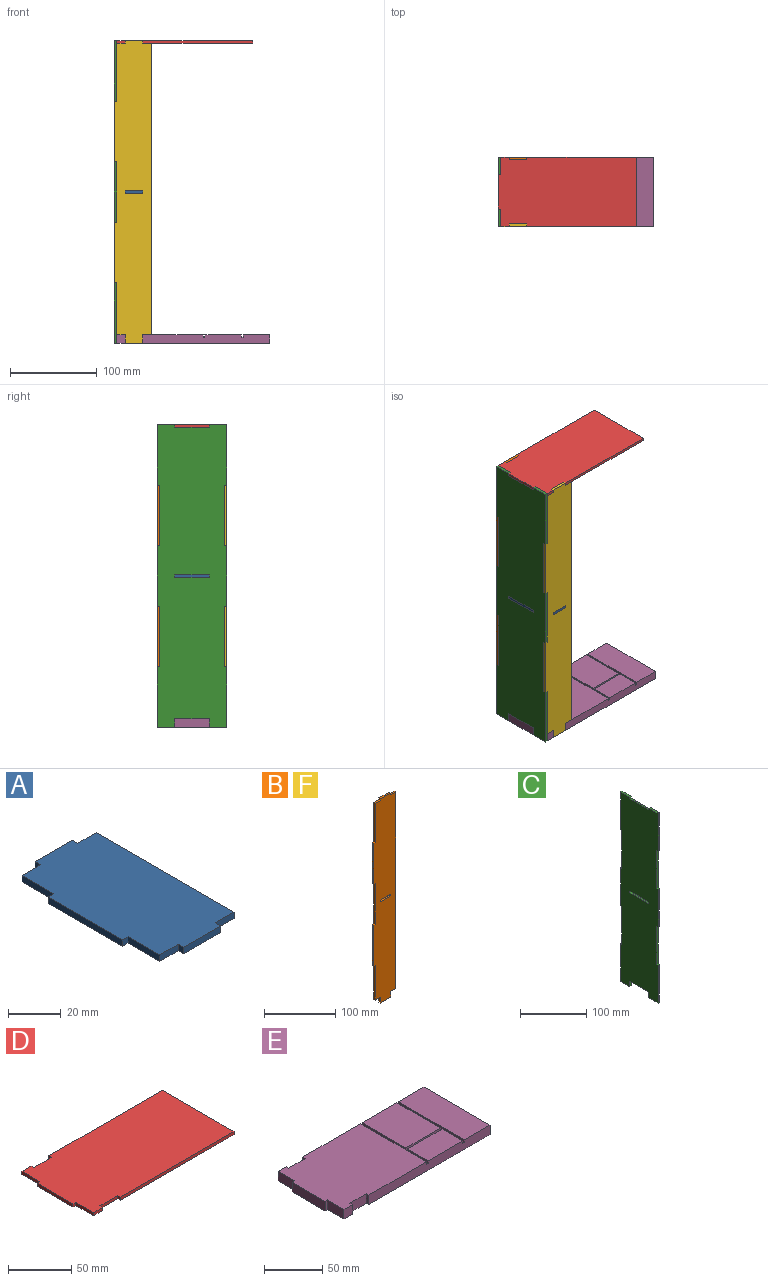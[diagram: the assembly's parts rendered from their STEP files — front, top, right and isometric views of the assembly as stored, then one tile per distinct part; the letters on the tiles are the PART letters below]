
ASSEMBLY  parts=6 mates=5
PART A: 18 faces, bbox 43x80x3 mm
  f0: plane 10x3mm, normal (0,-1,0), area 30mm2, adj f1,f15,f16,f17
  f1: plane 3x3mm, normal (-1,0,0), area 9mm2, adj f0,f2,f16,f17
  f2: plane 20x3mm, normal (0,-1,0), area 60mm2, adj f1,f3,f16,f17
  f3: plane 3x3mm, normal (1,0,0), area 9mm2, adj f2,f4,f16,f17
  f4: plane 10x3mm, normal (0,-1,0), area 30mm2, adj f3,f5,f16,f17
  f5: plane 74x3mm, normal (1,0,0), area 222mm2, adj f4,f6,f16,f17
  f6: plane 10x3mm, normal (0,1,0), area 30mm2, adj f5,f7,f16,f17
  f7: plane 3x3mm, normal (1,0,0), area 9mm2, adj f6,f8,f16,f17
  f8: plane 20x3mm, normal (0,1,0), area 60mm2, adj f7,f9,f16,f17
  f9: plane 3x3mm, normal (-1,0,0), area 9mm2, adj f8,f10,f16,f17
  f10: plane 10x3mm, normal (0,1,0), area 30mm2, adj f9,f11,f16,f17
  f11: plane 17x3mm, normal (-1,0,0), area 51mm2, adj f10,f12,f16,f17
  f12: plane 3x3mm, normal (0,1,0), area 9mm2, adj f11,f13,f16,f17
  f13: plane 40x3mm, normal (-1,0,0), area 120mm2, adj f12,f14,f16,f17
  f14: plane 3x3mm, normal (0,-1,0), area 9mm2, adj f13,f15,f16,f17
  f15: plane 17x3mm, normal (-1,0,0), area 51mm2, adj f0,f14,f16,f17
  f16: plane 80x43mm, normal (0,0,1), area 3200mm2, adj f0,f1,f2,f3,f4,f5,f6,f7
  f17: plane 80x43mm, normal (0,0,-1), area 3200mm2, adj f0,f1,f2,f3,f4,f5,f6,f7
PART B: 26 faces, bbox 43x3x350 mm
  f0: plane 10x3mm, normal (-1,0,0), area 30mm2, adj f1,f23,f24,f25
  f1: plane 20x3mm, normal (0,0,-1), area 60mm2, adj f0,f2,f24,f25
  f2: plane 10x3mm, normal (1,0,0), area 30mm2, adj f1,f3,f24,f25
  f3: plane 10x3mm, normal (0,0,-1), area 30mm2, adj f2,f4,f24,f25
  f4: plane 337x3mm, normal (1,0,0), area 1011mm2, adj f3,f5,f24,f25
  f5: plane 10x3mm, normal (0,0,1), area 30mm2, adj f4,f6,f24,f25
  f6: plane 3x3mm, normal (1,0,0), area 9mm2, adj f5,f7,f24,f25
  f7: plane 20x3mm, normal (0,0,1), area 60mm2, adj f6,f8,f24,f25
  f8: plane 3x3mm, normal (-1,0,0), area 9mm2, adj f7,f9,f24,f25
  f9: plane 10x3mm, normal (0,0,1), area 30mm2, adj f8,f10,f24,f25
  f10: plane 67x3mm, normal (-1,0,0), area 201mm2, adj f9,f11,f24,f25
  f11: plane 3x3mm, normal (0,0,1), area 9mm2, adj f10,f12,f24,f25
  f12: plane 70x3mm, normal (-1,0,0), area 210mm2, adj f11,f13,f24,f25
  f13: plane 3x3mm, normal (0,0,-1), area 9mm2, adj f12,f14,f24,f25
  f14: plane 70x3mm, normal (-1,0,0), area 210mm2, adj f13,f15,f24,f25
  f15: plane 3x3mm, normal (0,0,1), area 9mm2, adj f14,f16,f24,f25
  f16: plane 70x3mm, normal (-1,0,0), area 210mm2, adj f15,f17,f24,f25
  f17: plane 3x3mm, normal (0,0,-1), area 9mm2, adj f16,f18,f24,f25
  f18: plane 60x3mm, normal (-1,0,0), area 180mm2, adj f17,f23,f24,f25
  f19: plane 20x3mm, normal (0,0,-1), area 60mm2, adj f20,f22,f24,f25
  f20: plane 3x3mm, normal (-1,0,0), area 9mm2, adj f19,f21,f24,f25
  f21: plane 20x3mm, normal (0,0,1), area 60mm2, adj f20,f22,f24,f25
  f22: plane 3x3mm, normal (1,0,0), area 9mm2, adj f19,f21,f24,f25
  f23: plane 10x3mm, normal (0,0,-1), area 30mm2, adj f0,f18,f24,f25
  f24: plane 350x43mm, normal (0,1,0), area 14100mm2, adj f0,f1,f2,f3,f4,f5,f6,f7
  f25: plane 350x43mm, normal (0,-1,0), area 14100mm2, adj f0,f1,f2,f3,f4,f5,f6,f7
PART C: 34 faces, bbox 3x80x350 mm
  f0: plane 3x3mm, normal (0,1,0), area 9mm2, adj f1,f31,f32,f33
  f1: plane 20x3mm, normal (0,0,1), area 60mm2, adj f0,f2,f32,f33
  f2: plane 70x3mm, normal (0,-1,0), area 210mm2, adj f1,f3,f32,f33
  f3: plane 3x3mm, normal (0,0,-1), area 9mm2, adj f2,f4,f32,f33
  f4: plane 70x3mm, normal (0,-1,0), area 210mm2, adj f3,f5,f32,f33
  f5: plane 3x3mm, normal (0,0,1), area 9mm2, adj f4,f6,f32,f33
  f6: plane 70x3mm, normal (0,-1,0), area 210mm2, adj f5,f7,f32,f33
  f7: plane 3x3mm, normal (0,0,-1), area 9mm2, adj f6,f8,f32,f33
  f8: plane 70x3mm, normal (0,-1,0), area 210mm2, adj f7,f9,f32,f33
  f9: plane 3x3mm, normal (0,0,1), area 9mm2, adj f8,f10,f32,f33
  f10: plane 70x3mm, normal (0,-1,0), area 210mm2, adj f9,f11,f32,f33
  f11: plane 20x3mm, normal (0,0,-1), area 60mm2, adj f10,f12,f32,f33
  f12: plane 10x3mm, normal (0,1,0), area 30mm2, adj f11,f13,f32,f33
  f13: plane 40x3mm, normal (0,0,-1), area 120mm2, adj f12,f14,f32,f33
  f14: plane 10x3mm, normal (0,-1,0), area 30mm2, adj f13,f15,f32,f33
  f15: plane 20x3mm, normal (0,0,-1), area 60mm2, adj f14,f16,f32,f33
  f16: plane 70x3mm, normal (0,1,0), area 210mm2, adj f15,f17,f32,f33
  f17: plane 3x3mm, normal (0,0,1), area 9mm2, adj f16,f18,f32,f33
  f18: plane 70x3mm, normal (0,1,0), area 210mm2, adj f17,f19,f32,f33
  f19: plane 3x3mm, normal (0,0,-1), area 9mm2, adj f18,f20,f32,f33
  f20: plane 70x3mm, normal (0,1,0), area 210mm2, adj f19,f21,f32,f33
  f21: plane 3x3mm, normal (0,0,1), area 9mm2, adj f20,f22,f32,f33
  f22: plane 70x3mm, normal (0,1,0), area 210mm2, adj f21,f23,f32,f33
  f23: plane 3x3mm, normal (0,0,-1), area 9mm2, adj f22,f24,f32,f33
  f24: plane 70x3mm, normal (0,1,0), area 210mm2, adj f23,f25,f32,f33
  f25: plane 20x3mm, normal (0,0,1), area 60mm2, adj f24,f26,f32,f33
  f26: plane 3x3mm, normal (0,-1,0), area 9mm2, adj f25,f31,f32,f33
  f27: plane 40x3mm, normal (0,0,-1), area 120mm2, adj f28,f30,f32,f33
  f28: plane 3x3mm, normal (0,-1,0), area 9mm2, adj f27,f29,f32,f33
  f29: plane 40x3mm, normal (0,0,1), area 120mm2, adj f28,f30,f32,f33
  f30: plane 3x3mm, normal (0,1,0), area 9mm2, adj f27,f29,f32,f33
  f31: plane 40x3mm, normal (0,0,1), area 120mm2, adj f0,f26,f32,f33
  f32: plane 350x80mm, normal (-1,0,0), area 26520mm2, adj f0,f1,f2,f3,f4,f5,f6,f7
  f33: plane 350x80mm, normal (1,0,0), area 26520mm2, adj f0,f1,f2,f3,f4,f5,f6,f7
PART D: 18 faces, bbox 160x80x3 mm
  f0: plane 40x3mm, normal (-1,0,0), area 120mm2, adj f1,f15,f16,f17
  f1: plane 3x3mm, normal (0,-1,0), area 9mm2, adj f0,f2,f16,f17
  f2: plane 20x3mm, normal (-1,0,0), area 60mm2, adj f1,f3,f16,f17
  f3: plane 10x3mm, normal (0,-1,0), area 30mm2, adj f2,f4,f16,f17
  f4: plane 3x3mm, normal (1,0,0), area 9mm2, adj f3,f5,f16,f17
  f5: plane 20x3mm, normal (0,-1,0), area 60mm2, adj f4,f6,f16,f17
  f6: plane 3x3mm, normal (-1,0,0), area 9mm2, adj f5,f7,f16,f17
  f7: plane 127x3mm, normal (0,-1,0), area 381mm2, adj f6,f8,f16,f17
  f8: plane 80x3mm, normal (1,0,0), area 240mm2, adj f7,f9,f16,f17
  f9: plane 127x3mm, normal (0,1,0), area 381mm2, adj f8,f10,f16,f17
  f10: plane 3x3mm, normal (-1,0,0), area 9mm2, adj f9,f11,f16,f17
  f11: plane 20x3mm, normal (0,1,0), area 60mm2, adj f10,f12,f16,f17
  f12: plane 3x3mm, normal (1,0,0), area 9mm2, adj f11,f13,f16,f17
  f13: plane 10x3mm, normal (0,1,0), area 30mm2, adj f12,f14,f16,f17
  f14: plane 20x3mm, normal (-1,0,0), area 60mm2, adj f13,f15,f16,f17
  f15: plane 3x3mm, normal (0,1,0), area 9mm2, adj f0,f14,f16,f17
  f16: plane 160x80mm, normal (0,0,-1), area 12560mm2, adj f0,f1,f2,f3,f4,f5,f6,f7
  f17: plane 160x80mm, normal (0,0,1), area 12560mm2, adj f0,f1,f2,f3,f4,f5,f6,f7
PART E: 30 faces, bbox 180x80x10 mm
  f0: plane 147x10mm, normal (0,1,0), area 1458mm2, adj f2,f4,f12,f13,f19,f20,f21,f25
  f1: plane 147x10mm, normal (0,-1,0), area 1458mm2, adj f2,f3,f13,f14,f19,f20,f21,f22
  f2: plane 103x80mm, normal (0,0,1), area 8000mm2, adj f0,f1,f5,f6,f7,f8,f9,f10
  f3: plane 42x25mm, normal (0,0,1), area 1050mm2, adj f1,f22,f23,f24
  f4: plane 53x42mm, normal (0,0,1), area 2226mm2, adj f0,f26,f27,f28
  f5: plane 10x3mm, normal (0,-1,0), area 30mm2, adj f2,f6,f18,f20
  f6: plane 40x10mm, normal (-1,0,0), area 400mm2, adj f2,f5,f7,f20
  f7: plane 10x3mm, normal (0,1,0), area 30mm2, adj f2,f6,f8,f20
  f8: plane 20x10mm, normal (-1,0,0), area 200mm2, adj f2,f7,f9,f20
  f9: plane 10x10mm, normal (0,1,0), area 100mm2, adj f2,f8,f10,f20
  f10: plane 10x3mm, normal (1,0,0), area 30mm2, adj f2,f9,f11,f20
  f11: plane 20x10mm, normal (0,1,0), area 200mm2, adj f2,f10,f12,f20
  f12: plane 10x3mm, normal (-1,0,0), area 30mm2, adj f0,f2,f11,f20
  f13: plane 80x10mm, normal (1,0,0), area 800mm2, adj f0,f1,f19,f20
  f14: plane 10x3mm, normal (-1,0,0), area 30mm2, adj f1,f2,f15,f20
  f15: plane 20x10mm, normal (0,-1,0), area 200mm2, adj f2,f14,f16,f20
  f16: plane 10x3mm, normal (1,0,0), area 30mm2, adj f2,f15,f17,f20
  f17: plane 10x10mm, normal (0,-1,0), area 100mm2, adj f2,f16,f18,f20
  f18: plane 20x10mm, normal (-1,0,0), area 200mm2, adj f2,f5,f17,f20
  f19: plane 80x31mm, normal (0,0,1), area 2480mm2, adj f0,f1,f13,f25
  f20: plane 180x80mm, normal (0,0,-1), area 14160mm2, adj f0,f1,f5,f6,f7,f8,f9,f10
  f21: plane 80x3mm, normal (1,0,0), area 240mm2, adj f0,f1,f2,f29
  f22: plane 25x3mm, normal (-1,0,0), area 75mm2, adj f1,f3,f23,f29
  f23: plane 42x3mm, normal (0,1,0), area 126mm2, adj f3,f22,f24,f29
  f24: plane 25x3mm, normal (1,0,0), area 75mm2, adj f1,f3,f23,f29
  f25: plane 80x3mm, normal (-1,0,0), area 240mm2, adj f0,f1,f19,f29
  f26: plane 53x3mm, normal (1,0,0), area 159mm2, adj f0,f4,f27,f29
  f27: plane 42x3mm, normal (0,-1,0), area 126mm2, adj f4,f26,f28,f29
  f28: plane 53x3mm, normal (-1,0,0), area 159mm2, adj f0,f4,f27,f29
  f29: plane 80x46mm, normal (0,0,1), area 404mm2, adj f0,f1,f21,f22,f23,f24,f25,f26
PART F: same geometry as B
PLACE A t=(-9.02,17.65,-25.09)mm
PLACE B t=(-9.02,94.65,-25.09)mm
PLACE C t=(-9.02,17.65,-25.09)mm
PLACE D t=(-9.02,17.65,-25.09)mm
PLACE E t=(-9.02,17.65,-25.09)mm
PLACE F t=(-9.02,17.65,-25.09)mm
MATE fastened A.f16 <-> B.f19  axis (0,0,1) through (0.98,50.85,124.75)mm
MATE fastened C.f11 <-> E.f20  axis (0,0,1) through (-9.02,-26.15,-51.75)mm
MATE fastened D.f17 <-> C.f1  axis (0,0,1) through (-9.02,-26.15,298.25)mm
MATE fastened B.f1 <-> E.f20  axis (0,0,-1) through (0.98,53.85,-51.75)mm
MATE fastened F.f1 <-> E.f20  axis (0,0,-1) through (0.98,-23.15,-51.75)mm
